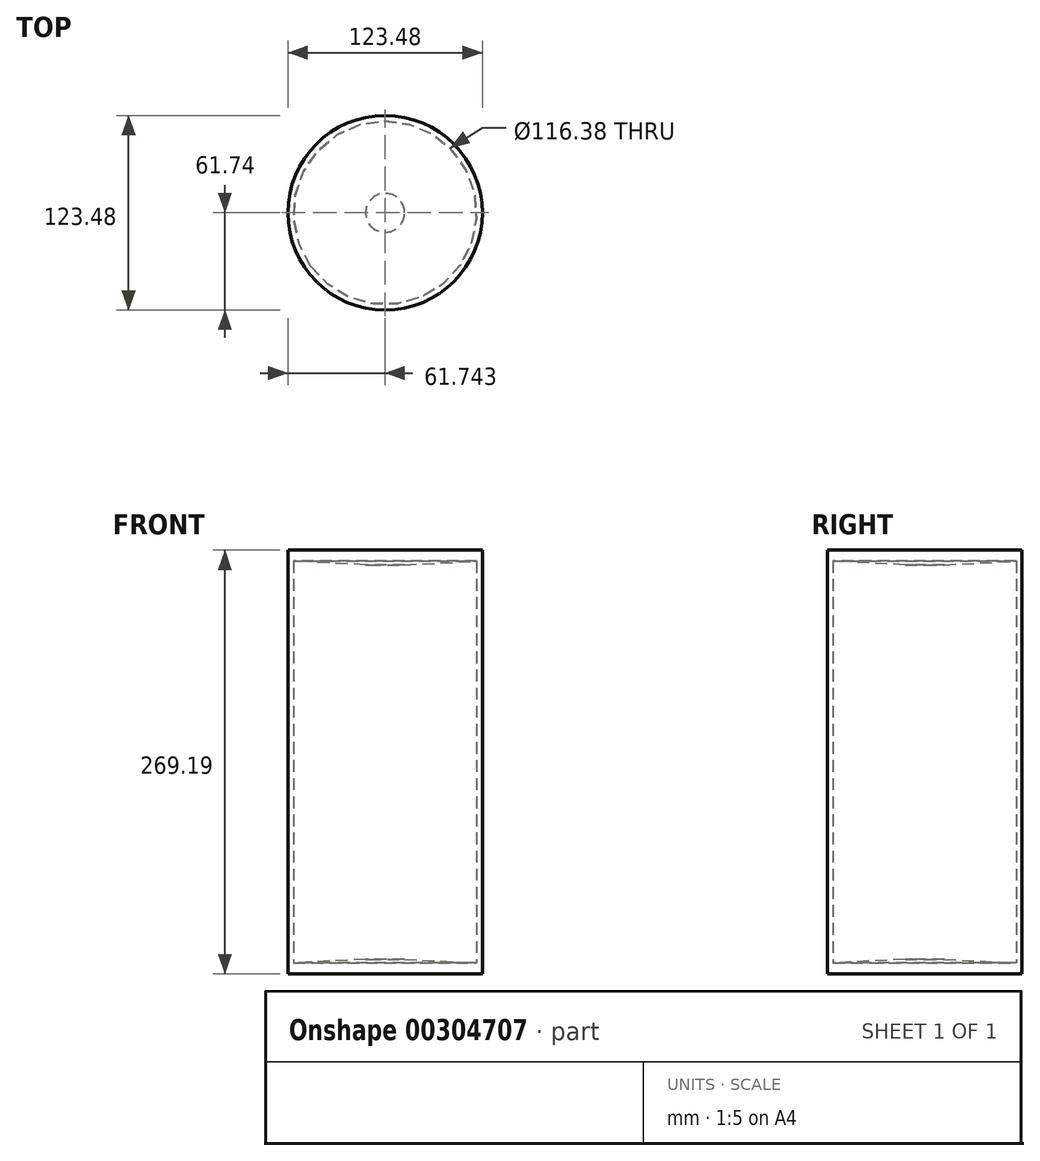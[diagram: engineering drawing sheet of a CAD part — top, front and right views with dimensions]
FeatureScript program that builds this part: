
annotation { "Feature Type Name" : "Feature", "Feature Type Description" : "" }
export const myFeature = defineFeature(function(context is Context, id is Id, definition is map)
    precondition{}
    {
        {
            var Q0;
            Q0=qCreatedBy(makeId("Front.planeOp"),FACE);
            var sketch = newSketch(context, id + "F0", { "sketchPlane" : qUnion([Q0])});
            skLineSegment(sketch, "E0", {"start": v(0, -54.61) * mm, "end": v(-58.24, -54.61) * mm});
            skLineSegment(sketch, "E1", {"start": v(-58.24, -54.61) * mm, "end": v(-58.24, -56.34) * mm});
            skLineSegment(sketch, "E2", {"start": v(-58.24, -56.34) * mm, "end": v(-61.74, -56.34) * mm});
            skLineSegment(sketch, "E3", {"start": v(-61.74, -56.34) * mm, "end": v(-61.74, -61.55) * mm});
            skLineSegment(sketch, "E4", {"start": v(-61.74, -61.55) * mm, "end": v(0, -61.55) * mm});
            skLineSegment(sketch, "E5", {"start": v(0, -54.61) * mm, "end": v(0, -61.55) * mm});
            skLineSegment(sketch, "E6", {"start": v(-58.24, -54.61) * mm, "end": v(-12.37, -52.2) * mm});
            skLineSegment(sketch, "E7", {"start": v(-12.37, -52.2) * mm, "end": v(0, -52.2) * mm});
            skLineSegment(sketch, "E8", {"start": v(0, -52.2) * mm, "end": v(0, -54.61) * mm});
            skLineSegment(sketch, "E9", {"start": v(-75.73, 75.48) * mm, "end": v(74.92, 75.48) * mm, "construction": true});
            skSolve(sketch);
        }
        {
            var Q0;
            Q0 = qSketchRegion(id + "F0", true);
            var Q1;
            Q1=sQuery(id+"F0.wireOp",EDGE,"E5");
            revolve(context, id + "F1", {"entities" : qUnion([Q0]), "axis" : qUnion([Q1]), "revolveType" : RevolveType.FULL});
        }
        {
            var Q0;
            Q0=qCreatedBy(makeId("Front.planeOp"),FACE);
            var sketch = newSketch(context, id + "F2", { "sketchPlane" : qUnion([Q0])});
            skLineSegment(sketch, "E10.bottom", {"start": v(-61.74, -56.33) * mm, "end": v(0, -56.33) * mm});
            skLineSegment(sketch, "E10.top", {"start": v(-61.74, 73.04) * mm, "end": v(0, 73.04) * mm});
            skLineSegment(sketch, "E10.left", {"start": v(-61.74, -56.33) * mm, "end": v(-61.74, 73.04) * mm});
            skLineSegment(sketch, "E11.bottom", {"start": v(-58.19, -56.33) * mm, "end": v(0, -56.33) * mm});
            skLineSegment(sketch, "E11.top", {"start": v(-58.19, 73.04) * mm, "end": v(0, 73.04) * mm});
            skLineSegment(sketch, "E11.left", {"start": v(-58.19, -56.33) * mm, "end": v(-58.19, 73.04) * mm});
            skLineSegment(sketch, "E12", {"start": v(0, -75.17) * mm, "end": v(0, 92.4) * mm, "construction": true});
            skPoint(sketch, "E12.startSnap0", {"position": v(0, -56.33) * mm});
            skPoint(sketch, "E12.endSnap0", {"position": v(0, 73.04) * mm});
            skPoint(sketch, "E13.trimOffspring.start.orphan", {"position": v(58.2, 73.04) * mm});
            skPoint(sketch, "E14.orphan", {"position": v(58.2, -56.33) * mm});
            skSolve(sketch);
        }
        {
            var Q0;
            Q0 = qSketchRegion(id + "F2", true);
            var Q1;
            Q1=sQuery(id+"F2.wireOp",EDGE,"E12");
            revolve(context, id + "F3", {"entities" : qUnion([Q0]), "axis" : qUnion([Q1]), "revolveType" : RevolveType.FULL});
        }
        {
            var Q0;
            Q0=makeQuery(id+"F1.opRevolve","SWEPT_BODY",BODY,{"disambiguationData":[OSD([sQuery(id+"F0.wireOp",EDGE,"E1"),sQuery(id+"F0.wireOp",EDGE,"E2"),sQuery(id+"F0.wireOp",EDGE,"E3"),sQuery(id+"F0.wireOp",EDGE,"E4"),sQuery(id+"F0.wireOp",EDGE,"E5"),sQuery(id+"F0.wireOp",EDGE,"E6"),sQuery(id+"F0.wireOp",EDGE,"E7"),sQuery(id+"F0.wireOp",EDGE,"E8")])]});
            var Q1;
            Q1=makeQuery(id+"F3.opRevolve","SWEPT_FACE",FACE,{"disambiguationData":[OSD([sQuery(id+"F2.wireOp",EDGE,"E10.top")])]});
            mirror(context, id + "F4", {"entities" : qUnion([Q0]), "mirrorPlane" : qUnion([Q1])});
        }
        {
            var Q0;
            Q0=makeQuery(id+"F3.opRevolve","SWEPT_BODY",BODY,{"disambiguationData":[OSD([sQuery(id+"F2.wireOp",EDGE,"E10.bottom"),sQuery(id+"F2.wireOp",EDGE,"E10.top"),sQuery(id+"F2.wireOp",EDGE,"E10.left"),sQuery(id+"F2.wireOp",EDGE,"E11.left")])]});
            var Q1;
            Q1=makeQuery(id+"F3.opRevolve","SWEPT_FACE",FACE,{"disambiguationData":[OSD([sQuery(id+"F2.wireOp",EDGE,"E10.top")])]});
            mirror(context, id + "F5", {"operationType" : NewBodyOperationType.ADD, "entities" : qUnion([Q0]), "mirrorPlane" : qUnion([Q1])});
        }
    });
